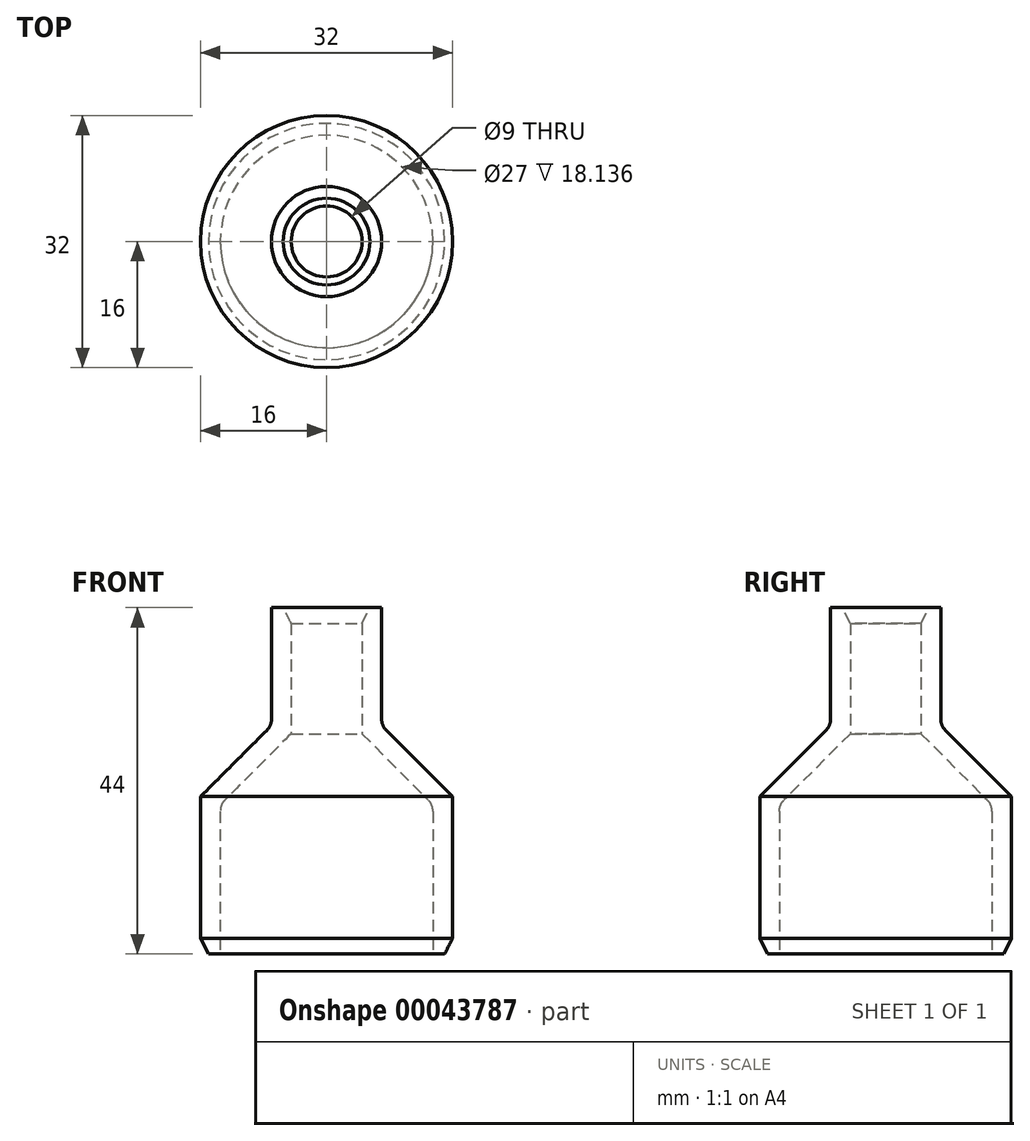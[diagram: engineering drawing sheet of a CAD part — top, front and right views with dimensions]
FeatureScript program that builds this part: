
annotation { "Feature Type Name" : "Feature", "Feature Type Description" : "" }
export const myFeature = defineFeature(function(context is Context, id is Id, definition is map)
    precondition{}
    {
        {
            var Q0;
            Q0=qCreatedBy(makeId("Front.planeOp"),FACE);
            var sketch = newSketch(context, id + "F0", { "sketchPlane" : qUnion([Q0])});
            skLineSegment(sketch, "E0", {"start": v(0, 44) * mm, "end": v(-7, 44) * mm});
            skLineSegment(sketch, "E1", {"start": v(-7, 44) * mm, "end": v(-7, 29) * mm});
            skLineSegment(sketch, "E2", {"start": v(-7, 29) * mm, "end": v(-16, 20) * mm});
            skLineSegment(sketch, "E3", {"start": v(-16, 20) * mm, "end": v(-16, 0) * mm});
            skLineSegment(sketch, "E4", {"start": v(-16, 0) * mm, "end": v(0, 0) * mm});
            skLineSegment(sketch, "E5", {"start": v(0, 0) * mm, "end": v(0, 44) * mm});
            skPoint(sketch, "E6", {"position": v(-4.5, 44) * mm});
            skSolve(sketch);
        }
        {
            var Q0;
            Q0=makeQuery(id+"F0.imprint","IMPRINT",FACE,{"disambiguationData":[TD([[makeQuery(id+"F0.imprint","IMPRINT",EDGE,{"derivedFrom":sQuery(id+"F0.wireOp",EDGE,"E0")}),1.0]])]});
            var Q1;
            Q1=sQuery(id+"F0.wireOp",EDGE,"E5");
            revolve(context, id + "F1", {"entities" : qUnion([Q0]), "axis" : qUnion([Q1]), "revolveType" : RevolveType.FULL});
        }
        {
            var Q0;
            Q0=makeQuery(id+"F1.opRevolve","SWEPT_FACE",FACE,{"disambiguationData":[OSD([sQuery(id+"F0.wireOp",EDGE,"E0")])]});
            var Q1;
            Q1=makeQuery(id+"F1.opRevolve","SWEPT_FACE",FACE,{"disambiguationData":[OSD([sQuery(id+"F0.wireOp",EDGE,"E4")])]});
            shell(context, id + "F2", {"entities" : qUnion([Q0, Q1]), "thickness" : 2.5 * mm});
        }
        {
            var Q0;
            Q0=makeQuery(id+"F1.opRevolve","SWEPT_EDGE",EDGE,{"disambiguationData":[OSD([sQuery(id+"F0.wireOp",EDGE,"E1"),sQuery(id+"F0.wireOp",EDGE,"E2")])]});
            var Q1;
            Q1=makeQuery(id+"F2.opShell","OFFSET_EDGE",EDGE,{"disambiguationData":[OSD([sQuery(id+"F0.wireOp",EDGE,"E2"),sQuery(id+"F0.wireOp",EDGE,"E3")])]});
            fillet(context, id + "F3", {"entities" : qUnion([Q0, Q1]), "radius" : 2 * mm, "tangentPropagation" : true, "allowEdgeOverflow" : false});
        }
        {
            var Q0;
            Q0=makeQuery(id+"F1.opRevolve","SWEPT_EDGE",EDGE,{"disambiguationData":[OSD([sQuery(id+"F0.wireOp",EDGE,"E3"),sQuery(id+"F0.wireOp",EDGE,"E4")])]});
            var Q1;
            Q1=makeQuery(id+"F2.opShell","OFFSET_EDGE",EDGE,{"disambiguationData":[OSD([sQuery(id+"F0.wireOp",EDGE,"E0"),sQuery(id+"F0.wireOp",EDGE,"E1")])]});
            chamfer(context, id + "F4", {"entities" : qUnion([Q0, Q1]), "chamferType" : ChamferType.TWO_OFFSETS, "width1" : 1 * mm, "oppositeDirection" : false, "width2" : 2 * mm, "tangentPropagation" : true});
        }
    });
